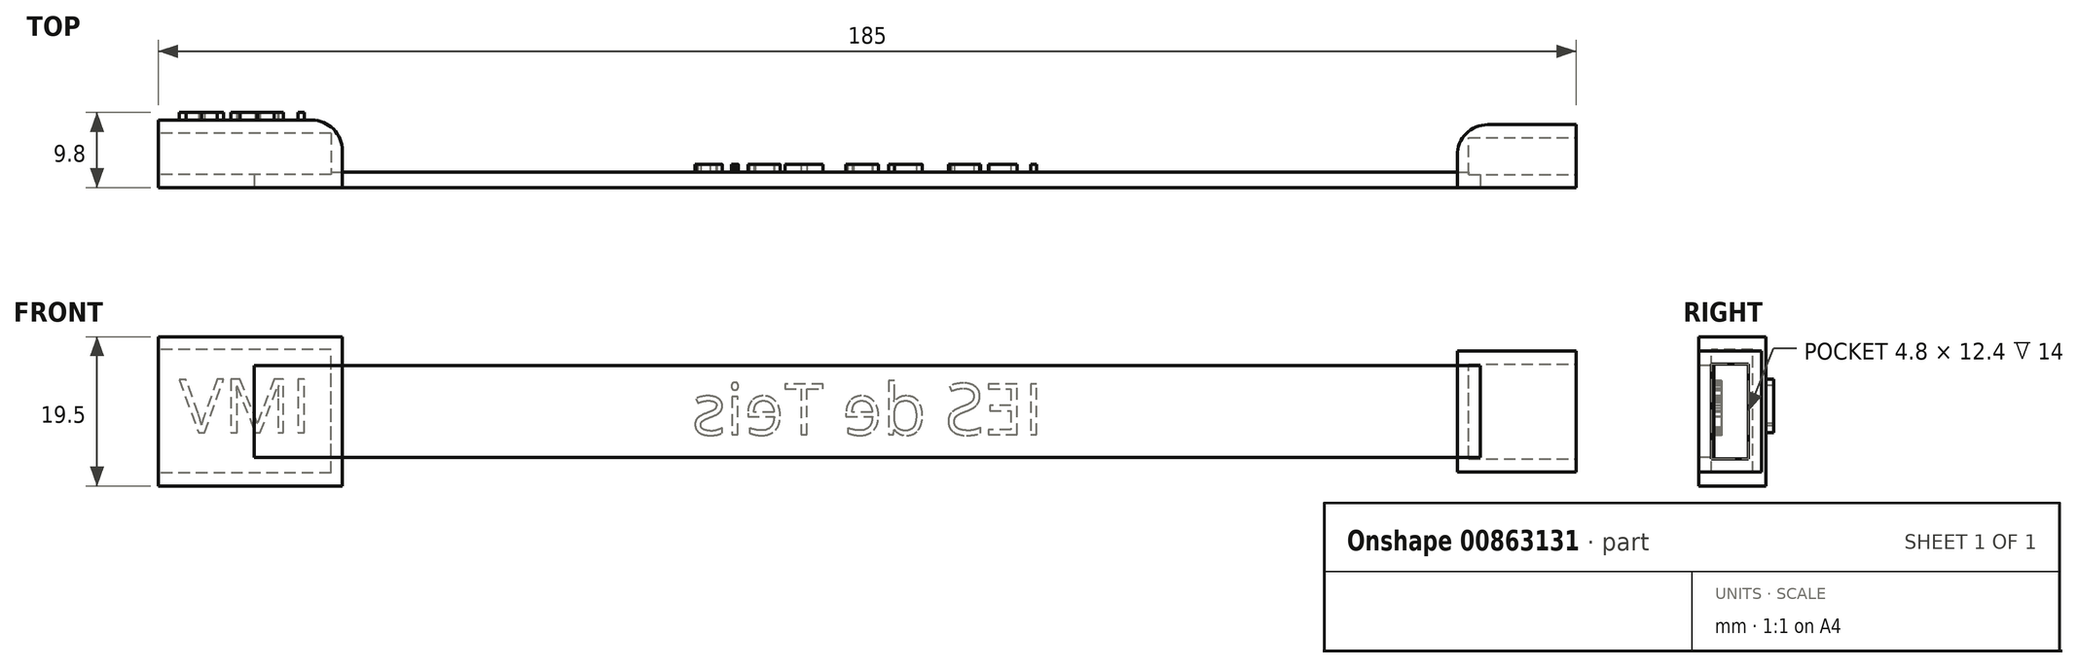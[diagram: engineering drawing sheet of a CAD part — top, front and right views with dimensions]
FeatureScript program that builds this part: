
annotation { "Feature Type Name" : "Feature", "Feature Type Description" : "" }
export const myFeature = defineFeature(function(context is Context, id is Id, definition is map)
    precondition{}
    {
        {
            var Q0;
            Q0=qCreatedBy(makeId("Front.planeOp"),FACE);
            var sketch = newSketch(context, id + "F0", { "sketchPlane" : qUnion([Q0])});
            skLineSegment(sketch, "E0.bottom", {"start": v(-80, 0) * mm, "end": v(80, 0) * mm});
            skLineSegment(sketch, "E0.top", {"start": v(-80, 12) * mm, "end": v(80, 12) * mm});
            skLineSegment(sketch, "E0.left", {"start": v(-80, 0) * mm, "end": v(-80, 12) * mm});
            skLineSegment(sketch, "E0.right", {"start": v(80, 0) * mm, "end": v(80, 12) * mm});
            skSolve(sketch);
        }
        {
            var Q0;
            Q0=qCreatedBy(makeId("Right.planeOp"),FACE);
            cPlane(context, id + "F1", {"entities" : qUnion([Q0]), "cplaneType" : CPlaneType.OFFSET, "offset" : 92.5 * mm, "width" : 150 * mm, "height" : 150 * mm});
        }
        {
            var Q0;
            Q0=qCreatedBy(makeId("Right.planeOp"),FACE);
            cPlane(context, id + "F2", {"entities" : qUnion([Q0]), "cplaneType" : CPlaneType.OFFSET, "offset" : 92.5 * mm, "oppositeDirection" : true, "width" : 150 * mm, "height" : 150 * mm});
        }
        {
            var Q0;
            Q0=qCreatedBy(id+"F1.planeOp",FACE);
            var sketch = newSketch(context, id + "F3", { "sketchPlane" : qUnion([Q0])});
            skLineSegment(sketch, "E1.bottom", {"start": v(0, -1.9) * mm, "end": v(8.2, -1.9) * mm});
            skLineSegment(sketch, "E1.top", {"start": v(0, 13.9) * mm, "end": v(8.2, 13.9) * mm});
            skLineSegment(sketch, "E1.left", {"start": v(0, -1.9) * mm, "end": v(0, 13.9) * mm});
            skLineSegment(sketch, "E1.right", {"start": v(8.2, -1.9) * mm, "end": v(8.2, 13.9) * mm});
            skSolve(sketch);
        }
        {
            var Q0;
            Q0=qCreatedBy(id+"F2.planeOp",FACE);
            var sketch = newSketch(context, id + "F4", { "sketchPlane" : qUnion([Q0])});
            skLineSegment(sketch, "E2.bottom", {"start": v(8.8, -3.75) * mm, "end": v(0, -3.75) * mm});
            skLineSegment(sketch, "E2.top", {"start": v(8.8, 15.75) * mm, "end": v(0, 15.75) * mm});
            skLineSegment(sketch, "E2.left", {"start": v(8.8, -3.75) * mm, "end": v(8.8, 15.75) * mm});
            skLineSegment(sketch, "E2.right", {"start": v(0, -3.75) * mm, "end": v(0, 15.75) * mm});
            skSolve(sketch);
        }
        {
            var Q0;
            Q0=makeQuery(id+"F3.imprint","IMPRINT",FACE,{"disambiguationData":[TD([[makeQuery(id+"F3.imprint","IMPRINT",EDGE,{"derivedFrom":sQuery(id+"F3.wireOp",EDGE,"E1.bottom")}),1.0]])]});
            var Q1;
            Q1=makeQuery(id+"F3.imprint","IMPRINT",FACE,{"disambiguationData":[TD([[makeQuery(id+"F3.imprint","IMPRINT",EDGE,{"derivedFrom":sQuery(id+"F3.wireOp",EDGE,"ULmGsHiY-Mv4B-d8Jg-noec-36pXMbrnfk32.bottom")}),1.0]])]});
            extrude(context, id + "F5", {"entities" : qUnion([Q0, Q1]), "oppositeDirection" : true, "depth" : 15.5 * mm, "offsetDistance" : 25 * mm});
        }
        {
            var Q0;
            Q0=qSketchRegion(id+"F4",true);
            var Q1;
            Q1=makeQuery(id+"F4.imprint","IMPRINT",FACE,{"disambiguationData":[TD([[makeQuery(id+"F4.imprint","IMPRINT",EDGE,{"derivedFrom":sQuery(id+"F4.wireOp",EDGE,"Hlka1Qad-GjJF-81ZI-ByxS-eIRTQnkwmmPv.bottom")}),1.0]])]});
            extrude(context, id + "F6", {"entities" : qUnion([Q0, Q1]), "depth" : 24 * mm, "offsetDistance" : 25 * mm});
        }
        {
            var Q0;
            Q0=qSketchRegion(id+"F0",true);
            extrude(context, id + "F7", {"entities" : qUnion([Q0]), "oppositeDirection" : true, "depth" : 2 * mm, "offsetDistance" : 25 * mm});
        }
        {
            var Q0;
            Q0=qCreatedBy(id+"F1.planeOp",FACE);
            var sketch = newSketch(context, id + "F8", { "sketchPlane" : qUnion([Q0])});
            skLineSegment(sketch, "E3.bottom", {"start": v(1.7, -0.2) * mm, "end": v(6.5, -0.2) * mm});
            skLineSegment(sketch, "E3.top", {"start": v(1.7, 12.2) * mm, "end": v(6.5, 12.2) * mm});
            skLineSegment(sketch, "E3.left", {"start": v(1.7, -0.2) * mm, "end": v(1.7, 12.2) * mm});
            skLineSegment(sketch, "E3.right", {"start": v(6.5, -0.2) * mm, "end": v(6.5, 12.2) * mm});
            skSolve(sketch);
        }
        {
            var Q0;
            Q0=qSketchRegion(id+"F8",true);
            extrude(context, id + "F9", {"entities" : qUnion([Q0]), "operationType" : NewBodyOperationType.REMOVE, "oppositeDirection" : true, "depth" : 14 * mm, "offsetDistance" : 25 * mm});
        }
        {
            var Q0;
            Q0=qCreatedBy(id+"F2.planeOp",FACE);
            var sketch = newSketch(context, id + "F10", { "sketchPlane" : qUnion([Q0])});
            skLineSegment(sketch, "E4.bottom", {"start": v(7.1, -2.05) * mm, "end": v(1.7, -2.05) * mm});
            skLineSegment(sketch, "E4.top", {"start": v(7.1, 14.05) * mm, "end": v(1.7, 14.05) * mm});
            skLineSegment(sketch, "E4.left", {"start": v(7.1, -2.05) * mm, "end": v(7.1, 14.05) * mm});
            skLineSegment(sketch, "E4.right", {"start": v(1.7, -2.05) * mm, "end": v(1.7, 14.05) * mm});
            skSolve(sketch);
        }
        {
            var Q0;
            Q0=qSketchRegion(id+"F10",true);
            extrude(context, id + "F11", {"entities" : qUnion([Q0]), "operationType" : NewBodyOperationType.REMOVE, "depth" : 22.5 * mm, "offsetDistance" : 25 * mm});
        }
        {
            var Q0;
            Q0=makeQuery(id+"F7.opExtrude","CAP_FACE",FACE,{"disambiguationData":[OSD([sQuery(id+"F0.wireOp",EDGE,"E0.bottom"),sQuery(id+"F0.wireOp",EDGE,"E0.top"),sQuery(id+"F0.wireOp",EDGE,"E0.left"),sQuery(id+"F0.wireOp",EDGE,"E0.right")])],"isStart":false});
            var sketch = newSketch(context, id + "F12", { "sketchPlane" : qUnion([Q0])});
            skText(sketch, "E5", { "text": "IES de Teis", "fontName": "OpenSans-Regular.ttf"});
            const initialGuessF12  = {"E5": [-0.02305, 0.00294, 1, 0, 0.00672]};
            skSetInitialGuess(sketch, initialGuessF12);
            skSolve(sketch);
        }
        {
            var Q0;
            Q0=qSketchRegion(id+"F12",true);
            extrude(context, id + "F13", {"entities" : qUnion([Q0]), "operationType" : NewBodyOperationType.ADD, "depth" : 1 * mm, "offsetDistance" : 25 * mm});
        }
        {
            var Q0;
            Q0=makeQuery(id+"F6.opExtrude","CAP_EDGE",EDGE,{"disambiguationData":[OSD([sQuery(id+"F4.wireOp",EDGE,"E2.left")])],"isStart":false});
            var Q1;
            Q1=makeQuery(id+"F5.opExtrude","CAP_EDGE",EDGE,{"disambiguationData":[OSD([sQuery(id+"F3.wireOp",EDGE,"E1.right")])],"isStart":false});
            fillet(context, id + "F14", {"entities" : qUnion([Q0, Q1]), "radius" : 4 * mm, "tangentPropagation" : true, "allowEdgeOverflow" : false});
        }
        {
            var Q0;
            Q0=makeQuery(id+"F6.opExtrude","SWEPT_FACE",FACE,{"disambiguationData":[OSD([sQuery(id+"F4.wireOp",EDGE,"E2.left")])]});
            var sketch = newSketch(context, id + "F15", { "sketchPlane" : qUnion([Q0])});
            skText(sketch, "E6", { "text": "IMV", "fontName": "OpenSans-Regular.ttf"});
            const initialGuessF15  = {"E6": [0.0725, 0.00325, 1, -0.00121, 0.007]};
            skSetInitialGuess(sketch, initialGuessF15);
            skSolve(sketch);
        }
        {
            var Q0;
            Q0=qSketchRegion(id+"F15",true);
            extrude(context, id + "F16", {"entities" : qUnion([Q0]), "operationType" : NewBodyOperationType.ADD, "depth" : 1 * mm, "offsetDistance" : 25 * mm});
        }
    });
